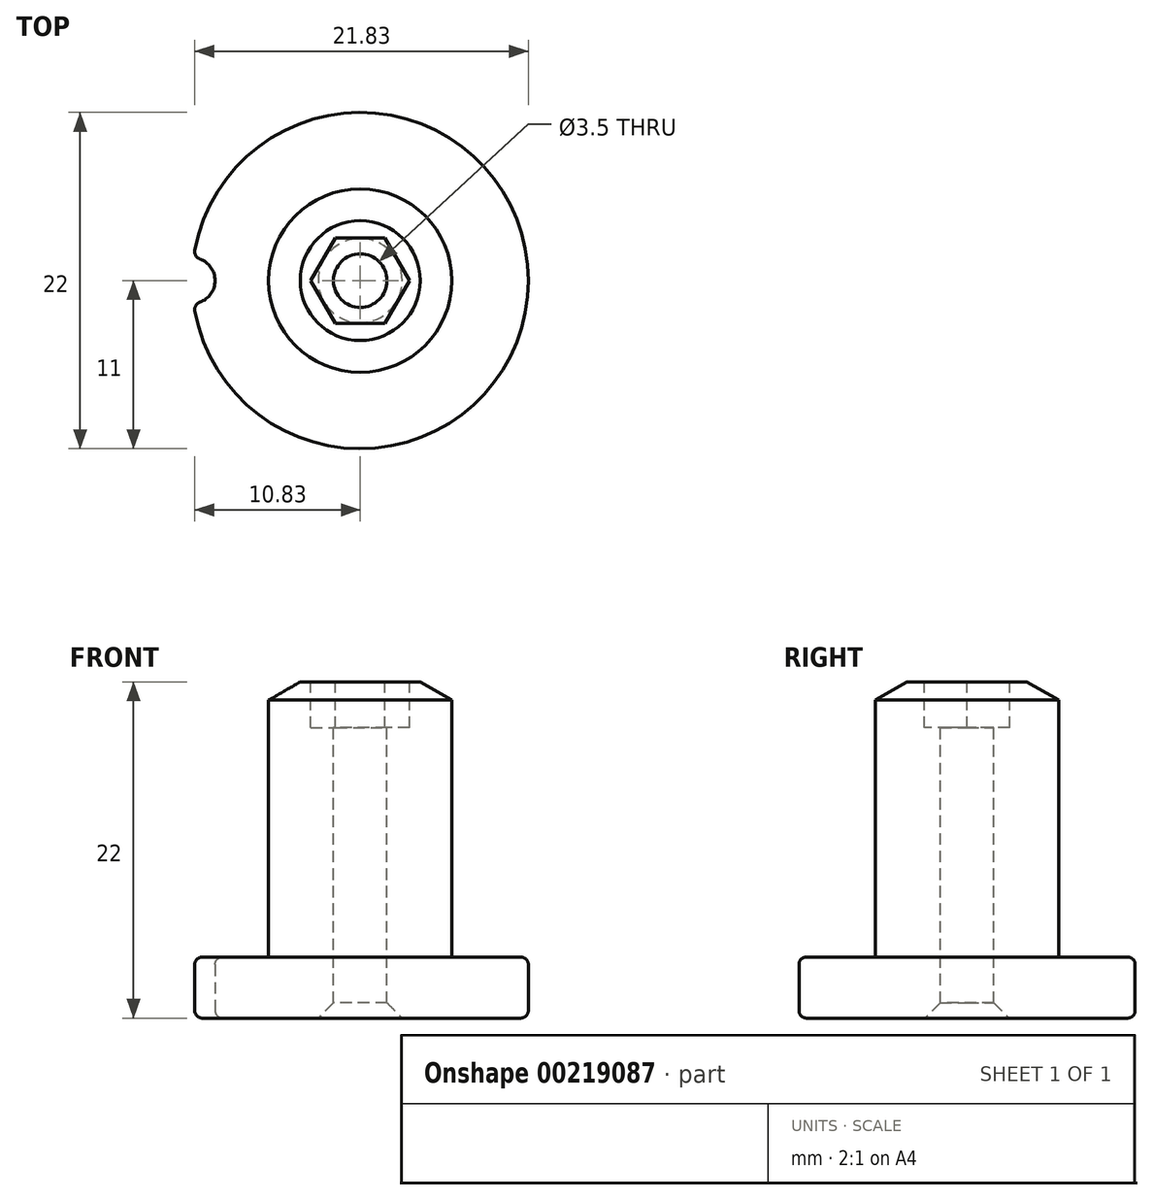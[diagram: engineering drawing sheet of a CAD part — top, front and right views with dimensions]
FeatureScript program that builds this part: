
annotation { "Feature Type Name" : "Feature", "Feature Type Description" : "" }
export const myFeature = defineFeature(function(context is Context, id is Id, definition is map)
    precondition{}
    {
        {
            var Q0;
            Q0=qCreatedBy(makeId("Front.planeOp"),FACE);
            var sketch = newSketch(context, id + "F0", { "sketchPlane" : qUnion([Q0])});
            skLineSegment(sketch, "E0", {"start": v(0, 22) * mm, "end": v(-6, 22) * mm});
            skLineSegment(sketch, "E1", {"start": v(-6, 22) * mm, "end": v(-6, 4) * mm});
            skLineSegment(sketch, "E2", {"start": v(-6, 4) * mm, "end": v(-11, 4) * mm});
            skLineSegment(sketch, "E3", {"start": v(-11, 4) * mm, "end": v(-11, 0) * mm});
            skLineSegment(sketch, "E4", {"start": v(-11, 0) * mm, "end": v(0, 0) * mm});
            skLineSegment(sketch, "E5", {"start": v(0, 0) * mm, "end": v(0, 22) * mm});
            skSolve(sketch);
        }
        {
            var Q0;
            Q0=makeQuery(id+"F0.imprint","IMPRINT",FACE,{"disambiguationData":[TD([[makeQuery(id+"F0.imprint","IMPRINT",EDGE,{"derivedFrom":sQuery(id+"F0.wireOp",EDGE,"E0")}),1.0]])]});
            var Q1;
            Q1=sQuery(id+"F0.wireOp",EDGE,"E5");
            revolve(context, id + "F1", {"entities" : qUnion([Q0]), "axis" : qUnion([Q1]), "revolveType" : RevolveType.FULL});
        }
        {
            var Q0;
            Q0=makeQuery(id+"F1.opRevolve","SWEPT_FACE",FACE,{"disambiguationData":[OSD([sQuery(id+"F0.wireOp",EDGE,"E0")])]});
            var sketch = newSketch(context, id + "F2", { "sketchPlane" : qUnion([Q0])});
            skCircle(sketch, "E6.cCircle", {"center": v(0, 0) * mm, "radius": 2.8 * mm, "construction": true});
            skLineSegment(sketch, "E6.0", {"start": v(3.23, 0) * mm, "end": v(1.62, -2.8) * mm});
            skLineSegment(sketch, "E6.1", {"start": v(1.62, -2.8) * mm, "end": v(-1.62, -2.8) * mm});
            skLineSegment(sketch, "E6.2", {"start": v(-1.62, -2.8) * mm, "end": v(-3.23, 0) * mm});
            skLineSegment(sketch, "E6.3", {"start": v(-3.23, 0) * mm, "end": v(-1.62, 2.8) * mm});
            skLineSegment(sketch, "E6.4", {"start": v(-1.62, 2.8) * mm, "end": v(1.62, 2.8) * mm});
            skLineSegment(sketch, "E6.5", {"start": v(1.62, 2.8) * mm, "end": v(3.23, 0) * mm});
            skPoint(sketch, "E6.0.midPoint", {"position": v(2.42, -1.4) * mm});
            skSolve(sketch);
        }
        {
            var Q0;
            Q0=makeQuery(id+"F2.imprint","IMPRINT",FACE,{"disambiguationData":[TD([[makeQuery(id+"F2.imprint","IMPRINT",EDGE,{"derivedFrom":sQuery(id+"F2.wireOp",EDGE,"E6.0")}),-1.0]])]});
            extrude(context, id + "F3", {"entities" : qUnion([Q0]), "operationType" : NewBodyOperationType.REMOVE, "oppositeDirection" : true, "depth" : 3 * mm});
        }
        {
            var Q0;
            Q0=makeQuery(id+"F3.boolean.opBoolean","COPY",FACE,{"derivedFrom":makeQuery(id+"F3.opExtrude","CAP_FACE",FACE,{"disambiguationData":[OSD([sQuery(id+"F2.wireOp",EDGE,"E6.0"),sQuery(id+"F2.wireOp",EDGE,"E6.1"),sQuery(id+"F2.wireOp",EDGE,"E6.2"),sQuery(id+"F2.wireOp",EDGE,"E6.3"),sQuery(id+"F2.wireOp",EDGE,"E6.4"),sQuery(id+"F2.wireOp",EDGE,"E6.5")])],"isStart":false})});
            var sketch = newSketch(context, id + "F4", { "sketchPlane" : qUnion([Q0])});
            skCircle(sketch, "E7", {"center": v(0, 0) * mm, "radius": 1.75 * mm});
            skSolve(sketch);
        }
        {
            var Q0;
            Q0=makeQuery(id+"F4.imprint","IMPRINT",FACE,{"disambiguationData":[TD([[makeQuery(id+"F4.imprint","IMPRINT",EDGE,{"derivedFrom":sQuery(id+"F4.wireOp",EDGE,"E7")}),1.0]])]});
            extrude(context, id + "F5", {"entities" : qUnion([Q0]), "operationType" : NewBodyOperationType.REMOVE, "endBound" : BoundingType.THROUGH_ALL, "oppositeDirection" : true, "depth" : 25 * mm});
        }
        {
            var Q0;
            Q0=qCreatedBy(makeId("Top.planeOp"),FACE);
            var sketch = newSketch(context, id + "F6", { "sketchPlane" : qUnion([Q0])});
            skCircle(sketch, "E8", {"center": v(-11, 0) * mm, "radius": 1.5 * mm});
            skSolve(sketch);
        }
        {
            var Q0;
            Q0=makeQuery(id+"F6.imprint","IMPRINT",FACE,{"disambiguationData":[TD([[makeQuery(id+"F6.imprint","IMPRINT",EDGE,{"derivedFrom":sQuery(id+"F6.wireOp",EDGE,"E8")}),1.0]])]});
            extrude(context, id + "F7", {"entities" : qUnion([Q0]), "operationType" : NewBodyOperationType.REMOVE, "depth" : 25 * mm});
        }
        {
            var Q0;
            Q0=makeQuery(id+"F7.boolean.opBoolean","INTERSECT",EDGE,{"disambiguationData":[OD(1.0)],"derivedFrom":[makeQuery(id+"F1.opRevolve","SWEPT_FACE",FACE,{"disambiguationData":[OSD([sQuery(id+"F0.wireOp",EDGE,"E3")])]}),makeQuery(id+"F7.opExtrude","SWEPT_FACE",FACE,{"disambiguationData":[OSD([sQuery(id+"F6.wireOp",EDGE,"E8")])]})]});
            var Q1;
            Q1=makeQuery(id+"F7.boolean.opBoolean","INTERSECT",EDGE,{"disambiguationData":[OD(0.0)],"derivedFrom":[makeQuery(id+"F1.opRevolve","SWEPT_FACE",FACE,{"disambiguationData":[OSD([sQuery(id+"F0.wireOp",EDGE,"E3")])]}),makeQuery(id+"F7.opExtrude","SWEPT_FACE",FACE,{"disambiguationData":[OSD([sQuery(id+"F6.wireOp",EDGE,"E8")])]})]});
            var Q2;
            Q2=makeQuery(id+"F7.boolean.opBoolean","INTERSECT",EDGE,{"derivedFrom":[makeQuery(id+"F1.opRevolve","SWEPT_FACE",FACE,{"disambiguationData":[OSD([sQuery(id+"F0.wireOp",EDGE,"E2")])]}),makeQuery(id+"F7.opExtrude","SWEPT_FACE",FACE,{"disambiguationData":[OSD([sQuery(id+"F6.wireOp",EDGE,"E8")])]})]});
            var Q3;
            Q3=makeQuery(id+"F7.boolean.opBoolean","COPY",EDGE,{"derivedFrom":makeQuery(id+"F7.opExtrude","CAP_EDGE",EDGE,{"disambiguationData":[OSD([sQuery(id+"F6.wireOp",EDGE,"E8")])],"isStart":true})});
            fillet(context, id + "F8", {"entities" : qUnion([Q0, Q1, Q2, Q3]), "radius" : .5 * mm, "tangentPropagation" : true, "allowEdgeOverflow" : false});
        }
        {
            var Q0;
            Q0=qCreatedBy(makeId("Front.planeOp"),FACE);
            var sketch = newSketch(context, id + "F9", { "sketchPlane" : qUnion([Q0])});
            skLineSegment(sketch, "E9", {"start": v(0, 46.76) * mm, "end": v(0, -22.25) * mm, "construction": true});
            skSolve(sketch);
        }
        {
            var Q0;
            Q0=makeQuery(id+"Fi5QTOe4qpchlEZ_1.1.F7.boolean.opBoolean","SPLIT",EDGE,{"disambiguationData":[OD(1.0)],"derivedFrom":makeQuery(id+"F1.opRevolve","SWEPT_EDGE",EDGE,{"disambiguationData":[OSD([sQuery(id+"F0.wireOp",EDGE,"E3"),sQuery(id+"F0.wireOp",EDGE,"E4")])]})});
            var Q1;
            Q1=makeQuery(id+"Fi5QTOe4qpchlEZ_1.1.F7.boolean.opBoolean","SPLIT",EDGE,{"disambiguationData":[OD(1.0)],"derivedFrom":makeQuery(id+"F1.opRevolve","SWEPT_EDGE",EDGE,{"disambiguationData":[OSD([sQuery(id+"F0.wireOp",EDGE,"E2"),sQuery(id+"F0.wireOp",EDGE,"E3")])]})});
            fillet(context, id + "F10", {"entities" : qUnion([Q0, Q1]), "radius" : .5 * mm, "tangentPropagation" : true, "allowEdgeOverflow" : false});
        }
        {
            var Q0;
            Q0=makeQuery(id+"F1.opRevolve","SWEPT_EDGE",EDGE,{"disambiguationData":[OSD([sQuery(id+"F0.wireOp",EDGE,"E0"),sQuery(id+"F0.wireOp",EDGE,"E1")])]});
            chamfer(context, id + "F11", {"entities" : qUnion([Q0]), "chamferType" : ChamferType.OFFSET_ANGLE, "width" : 1.2 * mm, "oppositeDirection" : false, "angle" : 60 * degree, "tangentPropagation" : true});
        }
        {
            var Q0;
            Q0=makeQuery(id+"F5.boolean.opBoolean","INTERSECT",EDGE,{"derivedFrom":[makeQuery(id+"F1.opRevolve","SWEPT_FACE",FACE,{"disambiguationData":[OSD([sQuery(id+"F0.wireOp",EDGE,"E4")])]}),makeQuery(id+"F5.opExtrude","SWEPT_FACE",FACE,{"disambiguationData":[OSD([sQuery(id+"F4.wireOp",EDGE,"E7")])]})]});
            chamfer(context, id + "F12", {"entities" : qUnion([Q0]), "width" : 1 * mm, "tangentPropagation" : true});
        }
    });
